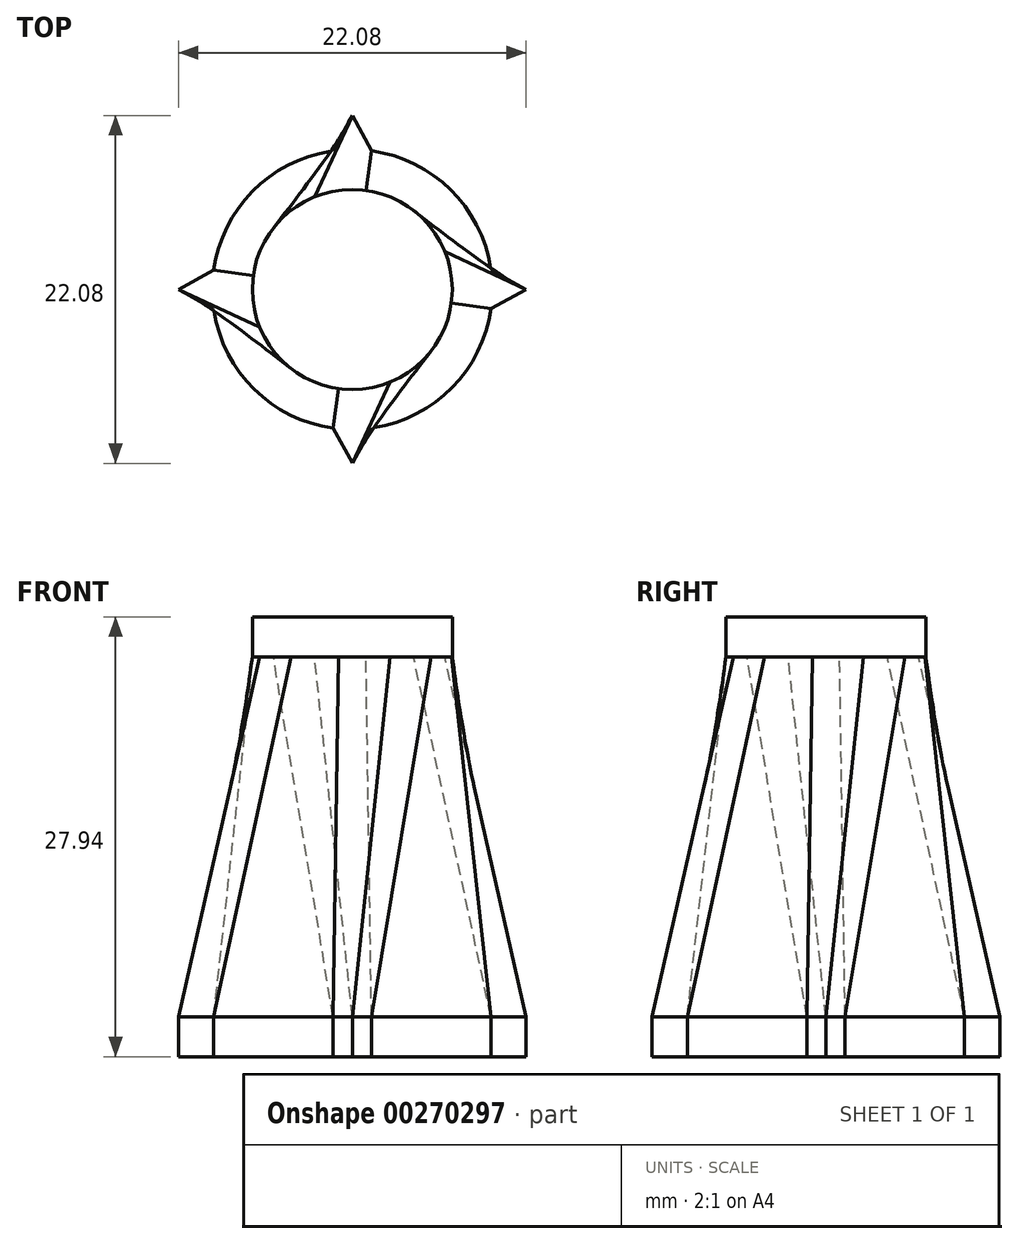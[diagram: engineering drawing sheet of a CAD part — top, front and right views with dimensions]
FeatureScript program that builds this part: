
annotation { "Feature Type Name" : "Feature", "Feature Type Description" : "" }
export const myFeature = defineFeature(function(context is Context, id is Id, definition is map)
    precondition{}
    {
        {
            var Q0;
            Q0=qCreatedBy(makeId("Top.planeOp"),FACE);
            var sketch = newSketch(context, id + "F0", { "sketchPlane" : qUnion([Q0])});
            skCircle(sketch, "E0", {"center": v(0, 0) * mm, "radius": 8.9 * mm});
            skLineSegment(sketch, "E1", {"start": v(1.22, 8.8) * mm, "end": v(0, 11.04) * mm});
            skLineSegment(sketch, "E2", {"start": v(0, 11.04) * mm, "end": v(-1.22, 8.8) * mm});
            skLineSegment(sketch, "E3.1.0", {"start": v(-11.04, 0) * mm, "end": v(-8.8, -1.22) * mm});
            skLineSegment(sketch, "E3.1.1", {"start": v(-8.8, 1.22) * mm, "end": v(-11.04, 0) * mm});
            skLineSegment(sketch, "E3.2.0", {"start": v(0, -11.04) * mm, "end": v(1.22, -8.8) * mm});
            skLineSegment(sketch, "E3.2.1", {"start": v(-1.22, -8.8) * mm, "end": v(0, -11.04) * mm});
            skLineSegment(sketch, "E3.3.0", {"start": v(11.04, 0) * mm, "end": v(8.8, 1.22) * mm});
            skLineSegment(sketch, "E3.3.1", {"start": v(8.8, -1.22) * mm, "end": v(11.04, 0) * mm});
            skSolve(sketch);
        }
        {
            var Q0;
            Q0=qCreatedBy(makeId("Top.planeOp"),FACE);
            cPlane(context, id + "F1", {"entities" : qUnion([Q0]), "cplaneType" : CPlaneType.OFFSET, "offset" : 25.4 * mm, "width" : 152.4 * mm, "height" : 152.4 * mm});
        }
        {
            var Q0;
            Q0=qCreatedBy(id+"F1.planeOp",FACE);
            var sketch = newSketch(context, id + "F2", { "sketchPlane" : qUnion([Q0])});
            skCircle(sketch, "E4", {"center": v(0, 0) * mm, "radius": 6.35 * mm});
            skSolve(sketch);
        }
        {
            var Q0;
            Q0=makeQuery(id+"F0.imprint","IMPRINT",FACE,{"disambiguationData":[TD([[makeQuery(id+"F0.imprint","IMPRINT",EDGE,{"derivedFrom":sQuery(id+"F0.wireOp",EDGE,"E0")}),1.0]])]});
            var Q1;
            {var subQ0=sQuery(id+"F0.wireOp",EDGE,"E1");Q1=makeQuery(id+"F0.imprint","IMPRINT",FACE,{"disambiguationData":[TD([[makeQuery(id+"F0.imprint","IMPRINT",EDGE,{"derivedFrom":subQ0}),1.0]])]});}
            var Q2;
            {var subQ0=sQuery(id+"F0.wireOp",EDGE,"E3.1.0");Q2=makeQuery(id+"F0.imprint","IMPRINT",FACE,{"disambiguationData":[TD([[makeQuery(id+"F0.imprint","IMPRINT",EDGE,{"derivedFrom":subQ0}),1.0]])]});}
            var Q3;
            {var subQ0=sQuery(id+"F0.wireOp",EDGE,"E3.3.0");Q3=makeQuery(id+"F0.imprint","IMPRINT",FACE,{"disambiguationData":[TD([[makeQuery(id+"F0.imprint","IMPRINT",EDGE,{"derivedFrom":subQ0}),1.0]])]});}
            var Q4;
            {var subQ0=sQuery(id+"F0.wireOp",EDGE,"E3.2.0");Q4=makeQuery(id+"F0.imprint","IMPRINT",FACE,{"disambiguationData":[TD([[makeQuery(id+"F0.imprint","IMPRINT",EDGE,{"derivedFrom":subQ0}),1.0]])]});}
            extrude(context, id + "F3", {"entities" : qUnion([Q0, Q1, Q2, Q3, Q4]), "depth" : 2.54 * mm});
        }
        {
            var Q0;
            Q0 = qSketchRegion(id + "F2", true);
            extrude(context, id + "F4", {"entities" : qUnion([Q0]), "operationType" : NewBodyOperationType.ADD, "depth" : 2.54 * mm});
        }
        {
            var Q0;
            Q0=makeQuery(id+"F3.opExtrude","CAP_FACE",FACE,{"disambiguationData":[OSD([sQuery(id+"F0.wireOp",EDGE,"E0")])],"isStart":false});
            var Q1;
            Q1=makeQuery(id+"F4.opExtrude","CAP_FACE",FACE,{"disambiguationData":[OSD([sQuery(id+"F2.wireOp",EDGE,"E4")])],"isStart":true});
            loft(context, id + "F5", {"sheetProfilesArray" : [{ "sheetProfileEntities" : qUnion([Q0]) }, { "sheetProfileEntities" : qUnion([Q1]) }]});
        }
    });
